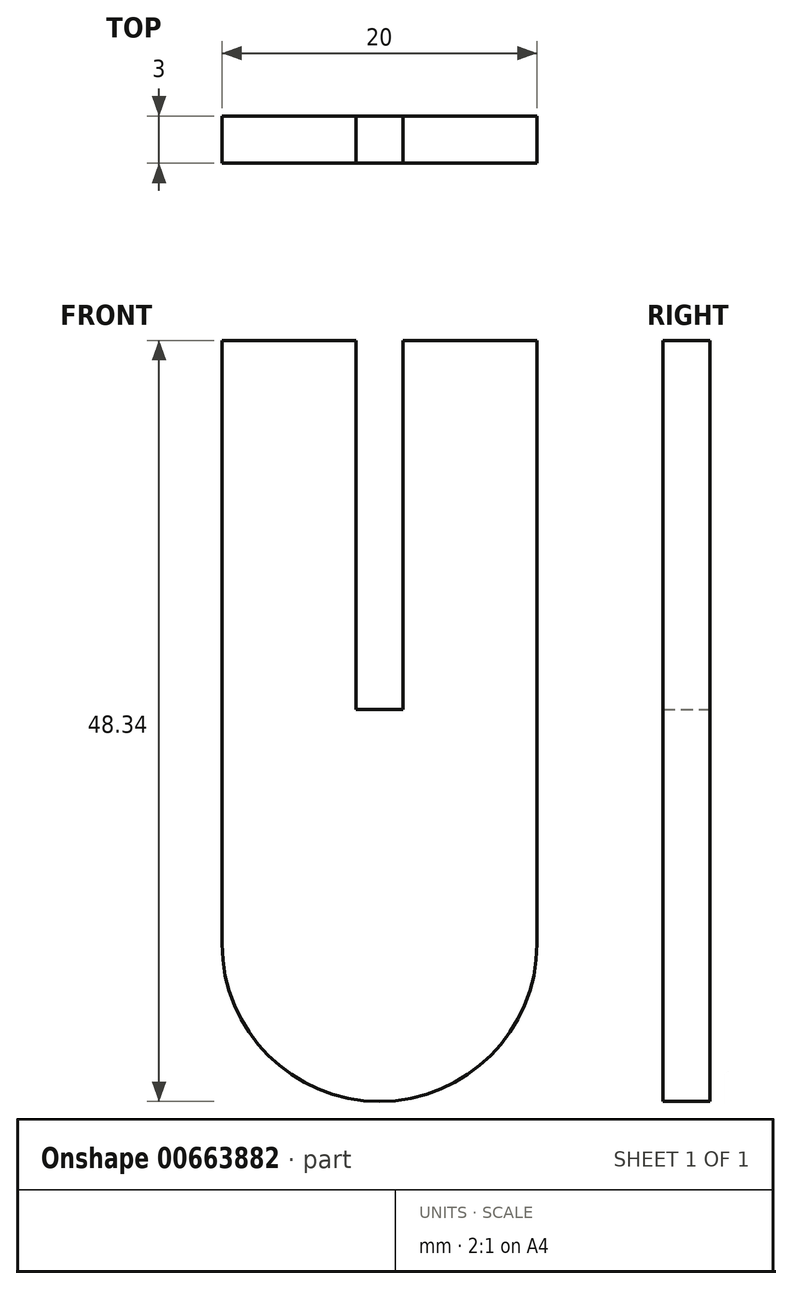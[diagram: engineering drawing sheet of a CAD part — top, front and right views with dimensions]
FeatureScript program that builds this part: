
annotation { "Feature Type Name" : "Feature", "Feature Type Description" : "" }
export const myFeature = defineFeature(function(context is Context, id is Id, definition is map)
    precondition{}
    {
        {
            var Q0;
            Q0=qCreatedBy(makeId("Front.planeOp"),FACE);
            var sketch = newSketch(context, id + "F0", { "sketchPlane" : qUnion([Q0])});
            skLineSegment(sketch, "E0.top", {"start": v(10, 19.17) * mm, "end": v(1.5, 19.17) * mm});
            skLineSegment(sketch, "E0.left", {"start": v(10, -19.17) * mm, "end": v(10, 19.17) * mm});
            skLineSegment(sketch, "E0.right", {"start": v(-10, -19.17) * mm, "end": v(-10, 19.17) * mm});
            skPoint(sketch, "E0.middle", {"position": v(0, 0) * mm});
            skArc(sketch, "E1", {"start": v(-10, -19.17) * mm, "mid": v(0, -29.17) * mm, "end": v(10, -19.17) * mm});
            skLineSegment(sketch, "E2.top", {"start": v(-1.5, -4.28) * mm, "end": v(1.5, -4.28) * mm});
            skLineSegment(sketch, "E2.left", {"start": v(-1.5, 19.17) * mm, "end": v(-1.5, -4.28) * mm});
            skLineSegment(sketch, "E2.right", {"start": v(1.5, 19.17) * mm, "end": v(1.5, -4.28) * mm});
            skLineSegment(sketch, "E3.trimOffspring", {"start": v(-1.5, 19.17) * mm, "end": v(-10, 19.17) * mm});
            skSolve(sketch);
        }
        {
            var Q0;
            Q0 = qSketchRegion(id + "F0", true);
            extrude(context, id + "F1", {"entities" : qUnion([Q0]), "depth" : 3 * mm, "offsetDistance" : 25 * mm});
        }
    });
